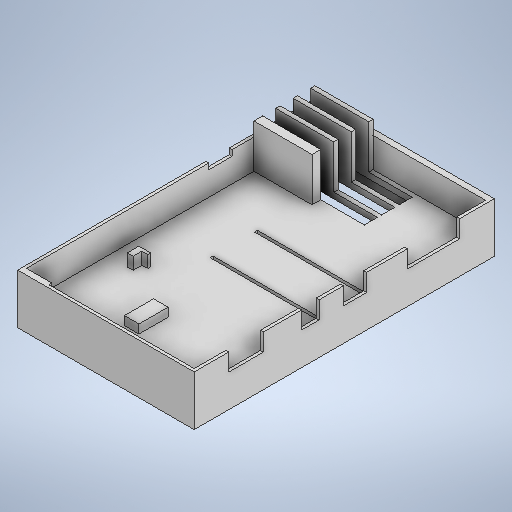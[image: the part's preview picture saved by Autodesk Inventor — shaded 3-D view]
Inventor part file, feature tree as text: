
AUTODESK INVENTOR PART (.ipt)
format: ipt  version: 2025.2 (Build 292293000, 293)  size: 739,328 bytes
history: native  units: mm
features: extrude x29, sketch x29
ambient origin geometry x8: Origin, YZ Plane, XZ Plane, XY Plane, X Axis, Y Axis, Z Axis, Center Point
bodies: Solid1 (feature_tree)
feature tree (58):
  extrude  "Extrusion1"  Depth=1.0mm
  extrude  "Extrusion2"  Depth=36.5mm
  extrude  "Extrusion3"  Depth=2.0mm TaperAngle=0.0deg
  extrude  "Extrusion4"  Depth=1.0mm
  extrude  "Extrusion5"  TaperAngle=0.0deg  [1 undecoded]
  extrude  "Extrusion6"  Depth=2.0mm
  extrude  "Extrusion7"  Depth=13.0mm
  extrude  "Extrusion8"  Depth=2.0mm
  extrude  "Extrusion9"  TaperAngle=0.0deg  [1 undecoded]
  extrude  "Extrusion10"  Depth=2.0mm
  extrude  "Extrusion11"  Depth=48.0mm
  extrude  "Extrusion12"  Depth=2.0mm
  extrude  "Extrusion13"  Depth=5.0mm
  extrude  "Extrusion14"  Depth=5.0mm
  extrude  "Extrusion15"  TaperAngle=0.0deg  [1 undecoded]
  extrude  "Extrusion16"  Depth=3.0mm
  extrude  "Extrusion17"  Depth=8.4mm
  extrude  "Extrusion18"  Depth=7.0mm
  extrude  "Extrusion19"  Depth=1.0mm
  extrude  "Extrusion20"  Depth=7.5mm
  extrude  "Extrusion21"  Depth=1.0mm
  extrude  "Extrusion22"  Depth=1.0mm
  extrude  "Extrusion23"  Depth=2.1mm
  extrude  "Extrusion24"  Depth=2.1mm
  extrude  "Extrusion25"  Depth=2.1mm TaperAngle=0.0deg
  extrude  "Extrusion26"  Depth=2.1mm TaperAngle=0.0deg
  extrude  "Extrusion27"  Depth=1.0mm
  extrude  "Extrusion28"  Depth=3.0mm
  extrude  "Extrusion29"  Depth=17.0mm
  sketch  "Sketch1"  dims[d0=36.5mm d1=1.0mm]
  sketch  "Sketch3"  dims[d2=1.0mm d3=36.5mm]
  sketch  "Sketch5"  dims[d4=14.298mm d5=2.0mm d6=0.0mm]
  sketch  "Sketch6"  dims[d7=5.0mm d8=1.0mm]
  sketch  "Sketch7"  dims[d9=0.0mm d10=0.0mm]
  sketch  "Sketch8"  dims[d11=4.2mm d12=0.0mm d13=2.0mm]
  sketch  "Sketch9"  dims[d14=2.0mm d15=13.0mm]
  sketch  "Sketch10"  dims[d16=4.2mm d17=0.0mm d18=2.0mm]
  sketch  "Sketch11"  dims[d19=2.0mm d20=0.0mm]
  sketch  "Sketch12"  dims[d21=30.0mm d22=2.0mm]
  sketch  "Sketch13"  dims[d23=4.0mm d24=48.0mm]
  sketch  "Sketch14"  dims[d25=0.0mm d26=2.0mm]
  sketch  "Sketch15"  dims[d27=5.0mm d28=5.0mm]
  sketch  "Sketch16"  dims[d29=15.0mm d30=5.0mm]
  sketch  "Sketch17"  dims[d31=3.0mm d32=0.0mm d33=0.0mm d34=0.0mm]
  sketch  "Sketch18"  dims[d35=6.0mm d36=3.0mm]
  sketch  "Sketch19"  dims[d37=6.0mm d38=0.0mm d39=8.4mm]
  sketch  "Sketch20"  dims[d40=10.2mm d41=7.0mm]
  sketch  "Sketch21"  dims[d42=11.9mm d43=1.0mm]
  sketch  "Sketch22"  dims[d44=15.0mm d45=7.5mm]
  sketch  "Sketch25"  dims[d46=5.0mm d47=1.0mm]
  sketch  "Sketch26"  dims[d48=1.0mm d49=1.0mm]
  sketch  "Sketch27"  dims[d50=1.0mm d51=2.1mm]
  sketch  "Sketch28"  dims[d52=2.1mm d53=2.1mm]
  sketch  "Sketch29"  dims[d54=2.1mm d55=2.1mm d56=0.0mm]
  sketch  "Sketch30"  dims[d57=12.0mm d58=2.1mm d59=0.0mm]
  sketch  "Sketch32"  dims[d60=2.0mm d61=1.0mm]
  sketch  "Sketch33"  dims[d62=4.2mm d63=0.0mm d64=3.0mm]
  sketch  "Sketch34"  dims[d65=20.0mm d66=17.0mm d67=3.0mm d68=3.0mm d69=3.0mm d70=3.0mm d71=3.0mm d72=3.0mm d73=15.0mm d74=0.0mm d75=35.0mm d76=35.0mm d77=12.0mm d78=0.0mm d79=15.0mm d80=15.0mm d81=0.0mm d82=2.0mm d83=4.2mm d84=0.0mm d85=0.0mm d86=0.0mm d87=2.0mm d88=1.0mm d89=6.0mm d90=0.0mm d91=1.0mm d92=2.0mm d93=2.0mm d94=5.0mm d95=0.0mm d96=36.0mm d97=1.0mm d98=5.0mm d99=0.0mm d100=0.0mm d101=22.0mm d102=22.0mm d103=2.0mm d104=2.0mm d105=5.5mm d106=0.0mm d107=2.0mm d108=4.2mm d109=4.2mm d110=2.0mm d111=1.0mm d112=5.0mm d113=0.0mm d114=15.1mm d115=1.0mm d116=1.0mm d117=4.0mm d118=0.0mm d119=12.0mm d120=2.0mm d121=0.0mm d124=8.0mm d125=2.0mm d126=0.0mm d127=1.5mm d128=1.5mm d129=1.5mm d130=10.0mm d131=0.0mm d132=1.0mm d133=10.0mm d134=0.0mm d135=4.2mm d136=0.0mm d137=4.2mm d138=0.0mm d139=2.0mm d140=0.0mm d141=1.0mm d142=5.0mm d143=0.0mm d144=3.0mm d145=5.0mm d146=0.0mm d147=10.2mm d148=0.0mm]
note: 3 required parameter values undecoded (feature->parameter linkage not recoverable at this tier; creation-order binding heuristic only, values carry confidence <= 0.55)
